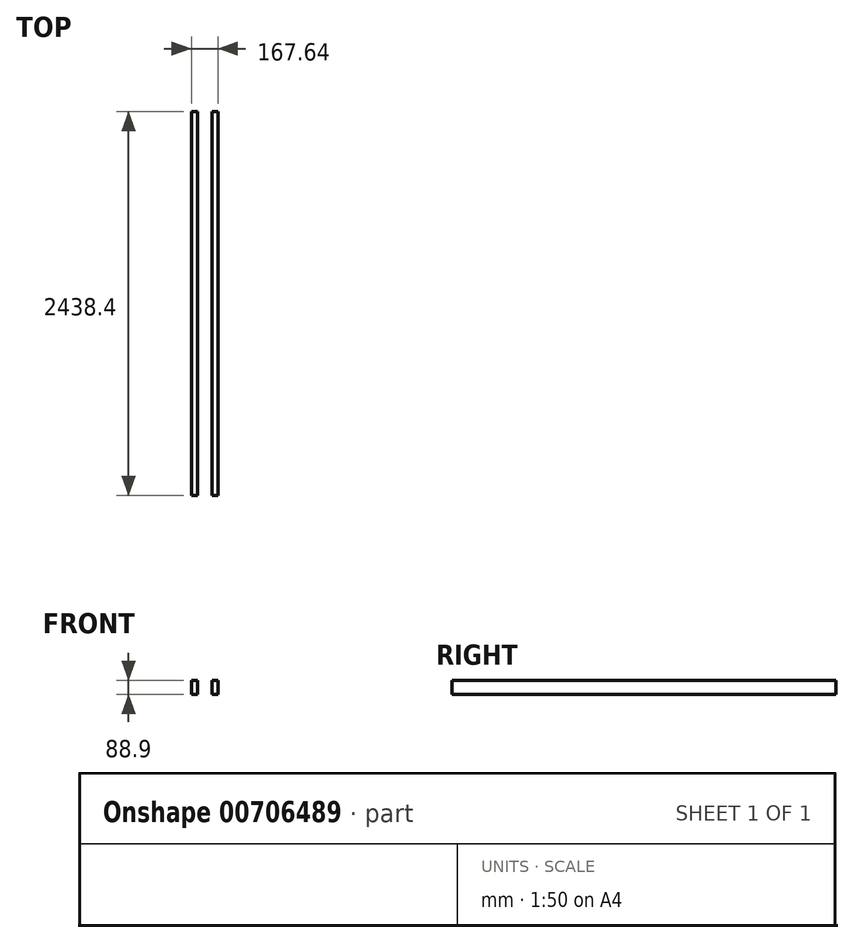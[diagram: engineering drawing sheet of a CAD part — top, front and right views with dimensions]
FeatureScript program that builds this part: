
annotation { "Feature Type Name" : "Feature", "Feature Type Description" : "" }
export const myFeature = defineFeature(function(context is Context, id is Id, definition is map)
    precondition{}
    {
        {
            var Q0;
            Q0=qCreatedBy(makeId("Front.planeOp"),FACE);
            var sketch = newSketch(context, id + "F0", { "sketchPlane" : qUnion([Q0])});
            skLineSegment(sketch, "E0.bottom", {"start": v(-90.71, 93.3) * mm, "end": v(-52.61, 93.3) * mm});
            skLineSegment(sketch, "E0.top", {"start": v(-90.71, 4.4) * mm, "end": v(-52.61, 4.4) * mm});
            skLineSegment(sketch, "E0.left", {"start": v(-90.71, 93.3) * mm, "end": v(-90.71, 4.4) * mm});
            skLineSegment(sketch, "E0.right", {"start": v(-52.61, 93.3) * mm, "end": v(-52.61, 4.4) * mm});
            skSolve(sketch);
        }
        {
            var Q0;
            Q0=makeQuery(id+"F0.imprint","IMPRINT",FACE,{"disambiguationData":[TD([[makeQuery(id+"F0.imprint","IMPRINT",EDGE,{"derivedFrom":sQuery(id+"F0.wireOp",EDGE,"E0.bottom")}),-1.0]])]});
            extrude(context, id + "F1", {"entities" : qUnion([Q0]), "depth" : 2438.4 * mm, "offsetDistance" : 25.4 * mm});
        }
        {
            var Q0;
            Q0=makeQuery(id+"F1.opExtrude","SWEPT_BODY",BODY,{"disambiguationData":[OSD([sQuery(id+"F0.wireOp",EDGE,"E0.bottom"),sQuery(id+"F0.wireOp",EDGE,"E0.top"),sQuery(id+"F0.wireOp",EDGE,"E0.left"),sQuery(id+"F0.wireOp",EDGE,"E0.right")])]});
            transform(context, id + "F2", {"entities" : qUnion([Q0]), "transformType" : TransformType.TRANSLATION_3D, "dx" : 129.54 * mm, "dy" : 0 * mm, "dz" : 0 * mm, "makeCopy" : true});
        }
        {
            var Q0;
            Q0=makeQuery(id+"F2.opPattern","COPY",FACE,{"derivedFrom":makeQuery(id+"F1.opExtrude","SWEPT_FACE",FACE,{"disambiguationData":[OSD([sQuery(id+"F0.wireOp",EDGE,"E0.top")])]}),"instanceName":"1"});
            cPlane(context, id + "F3", {"entities" : qUnion([Q0]), "cplaneType" : CPlaneType.OFFSET, "offset" : 25.4 * mm, "oppositeDirection" : true, "width" : 152.4 * mm, "height" : 152.4 * mm});
        }
    });
